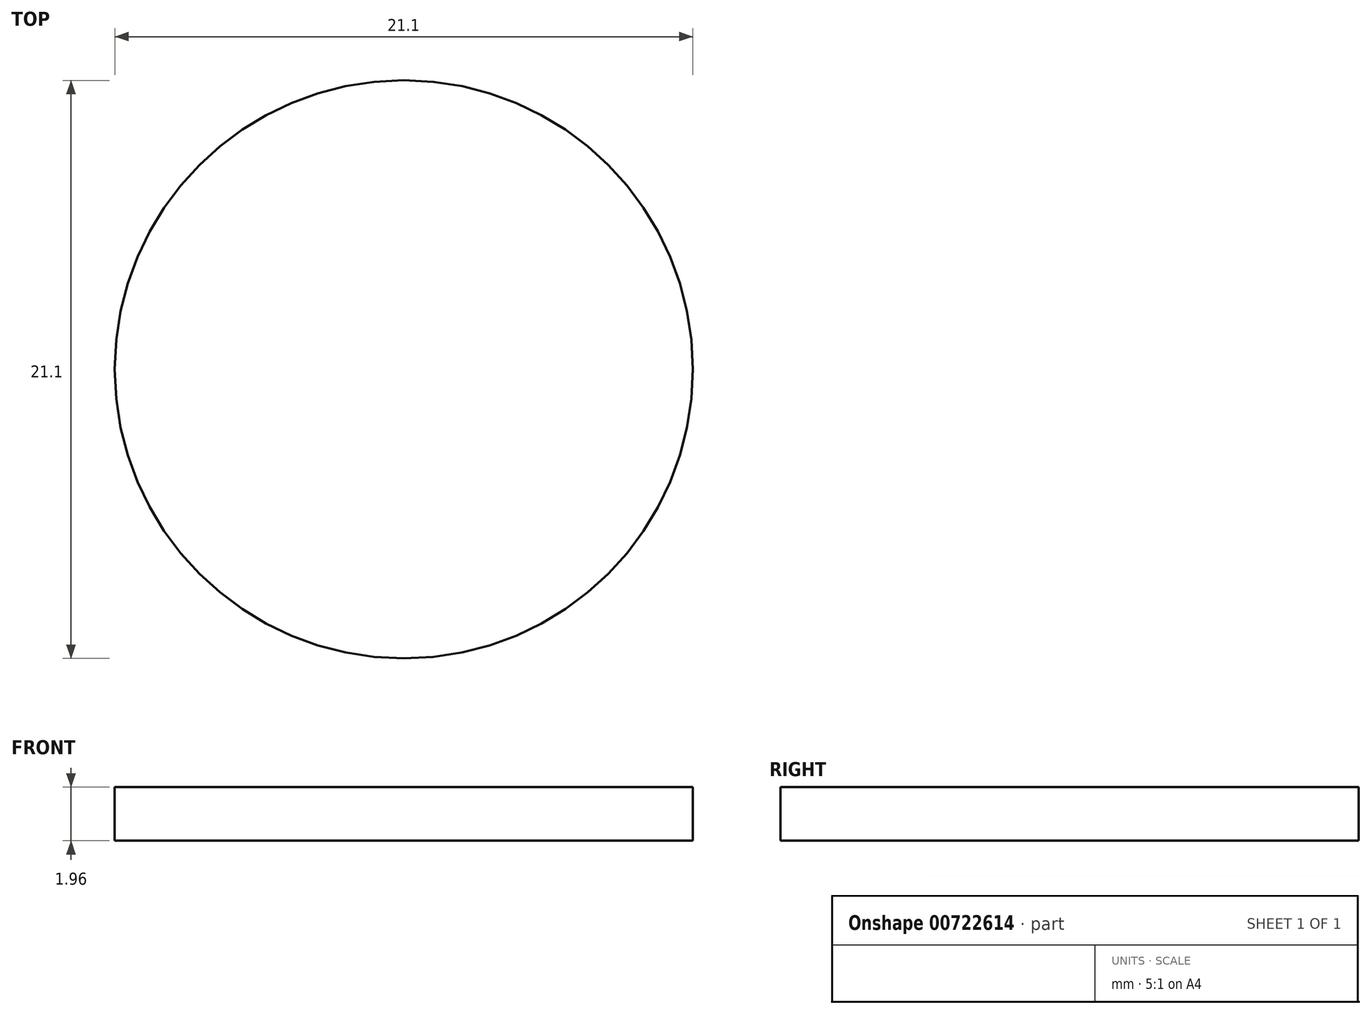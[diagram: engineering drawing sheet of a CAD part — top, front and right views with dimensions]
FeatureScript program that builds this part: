
annotation { "Feature Type Name" : "Feature", "Feature Type Description" : "" }
export const myFeature = defineFeature(function(context is Context, id is Id, definition is map)
    precondition{}
    {
        {
            var Q0;
            Q0=qCreatedBy(makeId("Top.planeOp"),FACE);
            var sketch = newSketch(context, id + "F0", { "sketchPlane" : qUnion([Q0])});
            skCircle(sketch, "E0", {"center": v(0, 0) * mm, "radius": 10.55 * mm});
            skSolve(sketch);
        }
        {
            var Q0;
            Q0 = qSketchRegion(id + "F0", true);
            extrude(context, id + "F1", {"entities" : qUnion([Q0]), "depth" : 1.96 * mm, "offsetDistance" : 25.4 * mm});
        }
        {
            var Q0;
            Q0=makeQuery(id+"F1.opExtrude","SWEPT_BODY",BODY,{"disambiguationData":[OSD([sQuery(id+"F0.wireOp",EDGE,"E0")])]});
            transform(context, id + "F2", {"entities" : qUnion([Q0]), "transformType" : TransformType.TRANSLATION_3D, "dx" : 0 * mm, "dy" : 0 * mm, "dz" : -1.96 * mm, "makeCopy" : false});
        }
    });
